SOLIDWORKS PART (.sldprt)
format: sldprt  version: not decoded by parser v0  size: 477,184 bytes
history: native  units: mm
features: plane x8, sketch x3, pattern_linear x2, material x1, extrude x1, cut_extrude x1, hole x1 + 1 further entry (+35 scaffold rows collapsed; 26 parser-record rows omitted)
feature tree (79):
  scaffold x35  (default folders/planes/origin — collapsed)
  material  "Material <not specified>"
  parser-record x26  (decoder bookkeeping rows leaked as tree rows — omitted from the tree; the rows remain in map.json)
  "Design Table"
  sketch  "Sketch1"  dims[WidthX=127.0mm HeightY=76.2mm CornerY=25.4mm CornerX=25.4mm]
  extrude  "Base Extrude"  Depth=4.7752mm ThickZ=4.7752mm
  sketch  "Sketch2"  dims[Hole1Diam=6.5278mm Hole1X=12.7mm Hole1Y=38.1mm]
  cut_extrude  "Hole1"  [1 undecoded]
  pattern_linear  "Hole1 Pattern"  Count1=5 Count2=1 Spacing1=25.4mm Spacing2=25.4mm NumberX=5 SpacingX=25.4mm NumberY=1 SpacingY=25.4mm
  sketch  "Sketch3"  dims[Hole2Diam=6.5278mm Hole2X=63.5mm Hole2Y=12.7mm]
  hole  "Hole2"  [1 undecoded]
  pattern_linear  "Hole2 Pattern"  Count1=1 Count2=2 Spacing1=25.4mm Spacing2=50.8mm NumberX=1 SpacingX=25.4mm NumberY=2 SpacingY=50.8mm
  plane  "Plane1"
  plane  "Plane2"
  plane  "Plane3"
  plane  "Plane4"
  plane  "Plane5"
  plane  "Plane6"
  plane  "Plane7"
  plane  "Plane8"
decode coverage: 6 of 8 modeling features carry decoded parameters; 1 rows unclassified (native names shown)
note: 2 parameter values undecoded
summary: [note 2] (x9 features) parser:v0:name_prior (class ref resolved by constrained assignment + name prior)
note: suppression state not decoded; provenance and decode notes live in map.json
